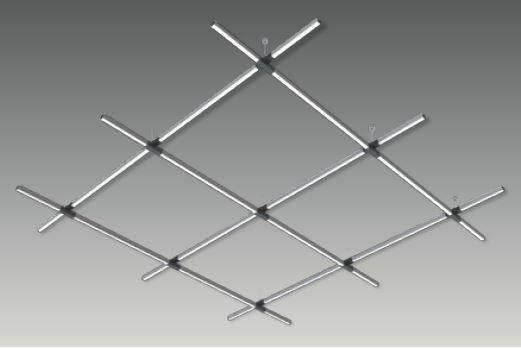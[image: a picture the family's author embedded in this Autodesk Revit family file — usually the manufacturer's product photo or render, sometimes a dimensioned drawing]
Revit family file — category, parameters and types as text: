
# Revit family: S 4545 PLG
name_source: partatom
category: Lighting Fixtures
revit_build: Autodesk Revit 2017 (Build: 20160225_1515(x64)
units: mm (PartAtom-declared; Revit-internal decimal feet)

## family parameters
Cut with Voids When Loaded = No
Host = Face
Light Source = Yes
Part Type = Normal
Room Calculation Point = No
Round Connector Dimension = Use Diameter
Shared = No

## types (2) — shared parameters
Color Filter = 16777215
Default Elevation = 1219 mm
Dimming Lamp Color Temperature Shift = <None>
Emit Shape Visible in Rendering = Yes
Emit from Rectangle Length = 1400 mm  [stored 4.59318 ft]
Emit from Rectangle Width = 40 mm  [stored 0.131234 ft]
Light Source Symbol Size = 610 mm
Manufacturer = ARLIGHT
Type Image = S 4545 PLG.JPG
Wattage Comments = 1104W

## type names (no varying parameters)
- SPLG.4545.1104.30
- SPLG.4545.1104.40

note: [stored X ft] marks values corroborated as IEEE doubles in the binary element streams (Revit-internal decimal feet)

## geometry (parser evidence)
native form markers: Sweep x8
no freeform markers — native parametric forms only
